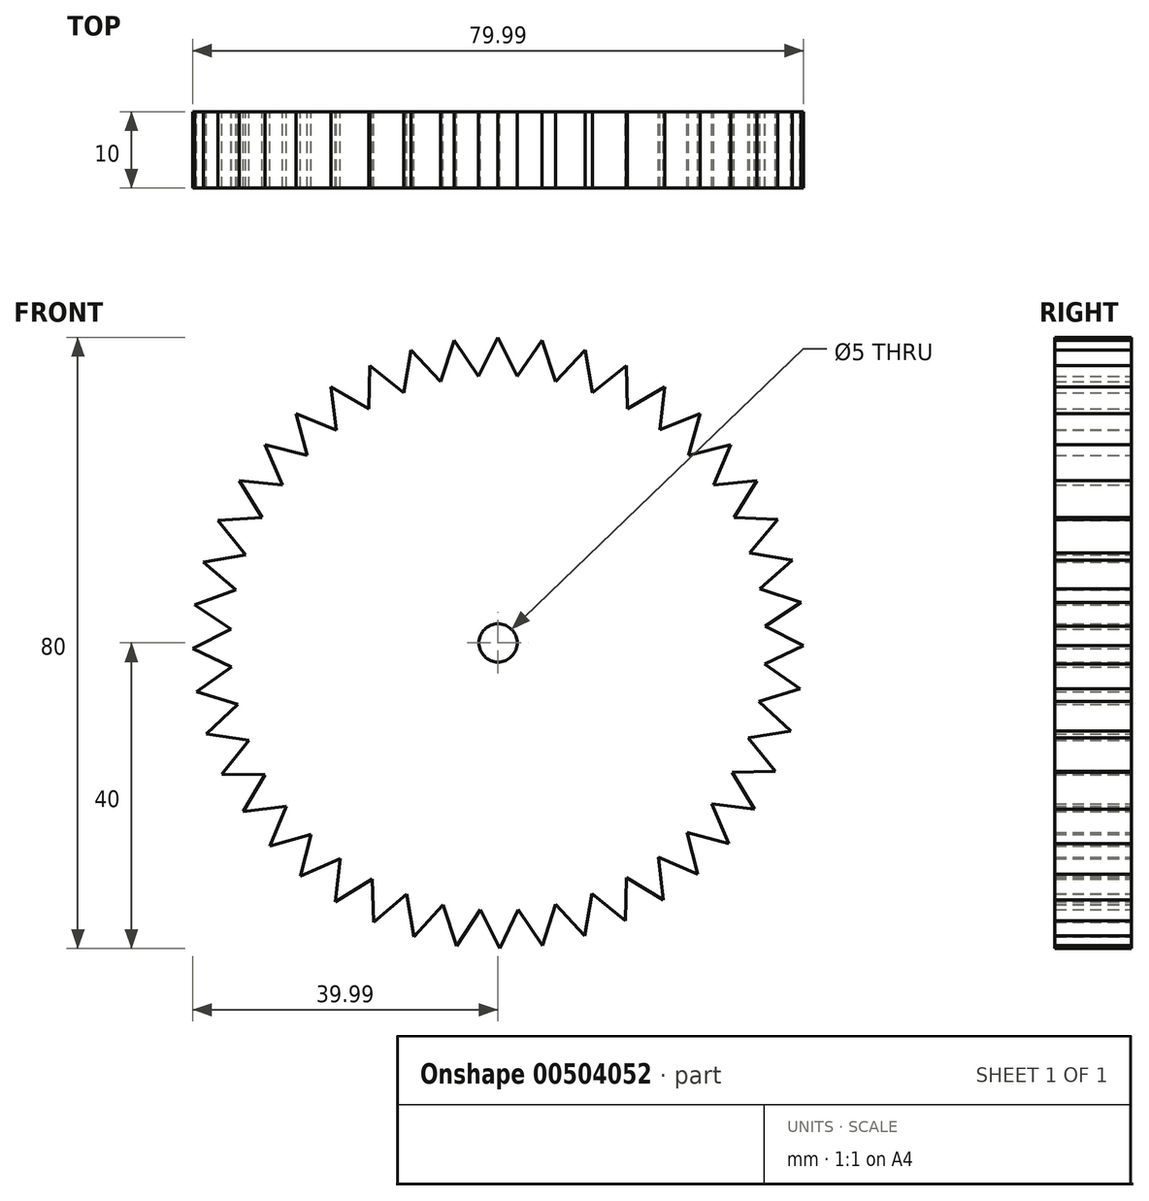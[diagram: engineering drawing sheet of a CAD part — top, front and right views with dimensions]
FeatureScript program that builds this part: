
annotation { "Feature Type Name" : "Feature", "Feature Type Description" : "" }
export const myFeature = defineFeature(function(context is Context, id is Id, definition is map)
    precondition{}
    {
        {
            var Q0;
            Q0=qCreatedBy(makeId("Front.planeOp"),FACE);
            var sketch = newSketch(context, id + "F0", { "sketchPlane" : qUnion([Q0])});
            skPoint(sketch, "E0.middle", {"position": v(0, 0) * mm});
            skCircle(sketch, "E1", {"center": v(0, 0) * mm, "radius": 40 * mm, "construction": true});
            skCircle(sketch, "E2", {"center": v(0, 0) * mm, "radius": 2.5 * mm});
            skLineSegment(sketch, "E3", {"start": v(0, 40) * mm, "end": v(2.52, 34.9) * mm});
            skLineSegment(sketch, "E4", {"start": v(2.52, 34.9) * mm, "end": v(5.75, 39.58) * mm});
            skLineSegment(sketch, "E5", {"start": v(5.75, 39.58) * mm, "end": v(7.52, 34.18) * mm});
            skLineSegment(sketch, "E6", {"start": v(7.52, 34.18) * mm, "end": v(11.39, 38.35) * mm});
            skLineSegment(sketch, "E7", {"start": v(11.39, 38.35) * mm, "end": v(12.36, 32.75) * mm});
            skLineSegment(sketch, "E8", {"start": v(12.36, 32.75) * mm, "end": v(16.78, 36.3) * mm});
            skLineSegment(sketch, "E9", {"start": v(16.78, 36.3) * mm, "end": v(16.94, 30.63) * mm});
            skLineSegment(sketch, "E10", {"start": v(16.94, 30.63) * mm, "end": v(21.83, 33.52) * mm});
            skLineSegment(sketch, "E11", {"start": v(21.83, 33.52) * mm, "end": v(21.17, 27.87) * mm});
            skLineSegment(sketch, "E12", {"start": v(21.17, 27.87) * mm, "end": v(26.42, 30.03) * mm});
            skLineSegment(sketch, "E13", {"start": v(26.42, 30.03) * mm, "end": v(24.95, 24.54) * mm});
            skCircle(sketch, "E14", {"center": v(0, 0) * mm, "radius": 35 * mm, "construction": true});
            skLineSegment(sketch, "E15", {"start": v(24.95, 24.54) * mm, "end": v(30.47, 25.92) * mm});
            skLineSegment(sketch, "E16", {"start": v(30.47, 25.92) * mm, "end": v(28.22, 20.7) * mm});
            skLineSegment(sketch, "E17", {"start": v(28.22, 20.7) * mm, "end": v(33.88, 21.27) * mm});
            skLineSegment(sketch, "E18", {"start": v(32.95, 11.8) * mm, "end": v(38.5, 10.85) * mm});
            skLineSegment(sketch, "E19", {"start": v(38.5, 10.85) * mm, "end": v(34.28, 7.09) * mm});
            skLineSegment(sketch, "E20", {"start": v(34.28, 7.09) * mm, "end": v(39.65, 5.3) * mm});
            skLineSegment(sketch, "E21", {"start": v(39.65, 5.3) * mm, "end": v(34.93, 2.18) * mm});
            skLineSegment(sketch, "E22", {"start": v(34.93, 2.18) * mm, "end": v(40, -0.34) * mm});
            skLineSegment(sketch, "E23", {"start": v(40, -0.34) * mm, "end": v(34.9, -2.77) * mm});
            skLineSegment(sketch, "E24", {"start": v(34.9, -2.77) * mm, "end": v(39.55, -5.98) * mm});
            skLineSegment(sketch, "E25", {"start": v(39.55, -5.98) * mm, "end": v(34.15, -7.67) * mm});
            skLineSegment(sketch, "E26", {"start": v(34.15, -7.67) * mm, "end": v(38.31, -11.5) * mm});
            skLineSegment(sketch, "E27", {"start": v(38.31, -11.5) * mm, "end": v(32.73, -12.4) * mm});
            skLineSegment(sketch, "E28", {"start": v(33.88, 21.27) * mm, "end": v(30.9, 16.42) * mm});
            skPoint(sketch, "E29.end.orphan", {"position": v(40, 0) * mm});
            skLineSegment(sketch, "E30", {"start": v(30.9, 16.42) * mm, "end": v(36.58, 16.17) * mm});
            skLineSegment(sketch, "E31", {"start": v(36.58, 16.17) * mm, "end": v(32.95, 11.8) * mm});
            skLineSegment(sketch, "E32", {"start": v(32.73, -12.4) * mm, "end": v(36.3, -16.79) * mm});
            skLineSegment(sketch, "E33", {"start": v(36.3, -16.79) * mm, "end": v(30.65, -16.9) * mm});
            skLineSegment(sketch, "E34", {"start": v(30.65, -16.9) * mm, "end": v(33.57, -21.74) * mm});
            skLineSegment(sketch, "E35", {"start": v(33.57, -21.74) * mm, "end": v(27.96, -21.06) * mm});
            skLineSegment(sketch, "E36", {"start": v(27.96, -21.06) * mm, "end": v(30.17, -26.26) * mm});
            skLineSegment(sketch, "E37", {"start": v(30.17, -26.26) * mm, "end": v(24.7, -24.8) * mm});
            skLineSegment(sketch, "E38", {"start": v(24.7, -24.8) * mm, "end": v(26.16, -30.26) * mm});
            skLineSegment(sketch, "E39", {"start": v(26.16, -30.26) * mm, "end": v(20.96, -28.03) * mm});
            skLineSegment(sketch, "E40", {"start": v(20.96, -28.03) * mm, "end": v(21.63, -33.65) * mm});
            skLineSegment(sketch, "E41", {"start": v(21.63, -33.65) * mm, "end": v(16.8, -30.7) * mm});
            skLineSegment(sketch, "E42", {"start": v(16.8, -30.7) * mm, "end": v(16.67, -36.36) * mm});
            skLineSegment(sketch, "E43", {"start": v(16.67, -36.36) * mm, "end": v(12.3, -32.77) * mm});
            skLineSegment(sketch, "E44", {"start": v(12.3, -32.77) * mm, "end": v(11.37, -38.35) * mm});
            skLineSegment(sketch, "E45", {"start": v(11.37, -38.35) * mm, "end": v(7.55, -34.18) * mm});
            skLineSegment(sketch, "E46", {"start": v(7.55, -34.18) * mm, "end": v(5.85, -39.57) * mm});
            skLineSegment(sketch, "E47", {"start": v(5.85, -39.57) * mm, "end": v(2.65, -34.9) * mm});
            skLineSegment(sketch, "E48", {"start": v(2.65, -34.9) * mm, "end": v(0.2, -40) * mm});
            skLineSegment(sketch, "E49", {"start": v(0.2, -40) * mm, "end": v(-2.3, -34.92) * mm});
            skLineSegment(sketch, "E50", {"start": v(-2.3, -34.92) * mm, "end": v(-5.44, -39.63) * mm});
            skLineSegment(sketch, "E51", {"start": v(-5.44, -39.63) * mm, "end": v(-7.2, -34.25) * mm});
            skLineSegment(sketch, "E52", {"start": v(-7.2, -34.25) * mm, "end": v(-10.98, -38.46) * mm});
            skLineSegment(sketch, "E53", {"start": v(-10.98, -38.46) * mm, "end": v(-11.96, -32.9) * mm});
            skLineSegment(sketch, "E54", {"start": v(-11.96, -32.9) * mm, "end": v(-16.3, -36.53) * mm});
            skLineSegment(sketch, "E55", {"start": v(-16.3, -36.53) * mm, "end": v(-16.48, -30.88) * mm});
            skLineSegment(sketch, "E56", {"start": v(-16.48, -30.88) * mm, "end": v(-21.29, -33.87) * mm});
            skLineSegment(sketch, "E57", {"start": v(-21.29, -33.87) * mm, "end": v(-20.67, -28.24) * mm});
            skLineSegment(sketch, "E58", {"start": v(-20.67, -28.24) * mm, "end": v(-25.85, -30.52) * mm});
            skLineSegment(sketch, "E59", {"start": v(-25.85, -30.52) * mm, "end": v(-24.45, -25.04) * mm});
            skLineSegment(sketch, "E60", {"start": v(-24.45, -25.04) * mm, "end": v(-29.9, -26.57) * mm});
            skLineSegment(sketch, "E61", {"start": v(-29.9, -26.57) * mm, "end": v(-27.74, -21.34) * mm});
            skLineSegment(sketch, "E62", {"start": v(-27.74, -21.34) * mm, "end": v(-33.35, -22.09) * mm});
            skLineSegment(sketch, "E63", {"start": v(-33.35, -22.09) * mm, "end": v(-30.47, -17.21) * mm});
            skLineSegment(sketch, "E64", {"start": v(-30.47, -17.21) * mm, "end": v(-36.13, -17.16) * mm});
            skLineSegment(sketch, "E65", {"start": v(-36.13, -17.16) * mm, "end": v(-32.6, -12.74) * mm});
            skLineSegment(sketch, "E66", {"start": v(-32.6, -12.74) * mm, "end": v(-38.2, -11.9) * mm});
            skLineSegment(sketch, "E67", {"start": v(-38.2, -11.9) * mm, "end": v(-34.07, -8.02) * mm});
            skLineSegment(sketch, "E68", {"start": v(-34.07, -8.02) * mm, "end": v(-39.49, -6.38) * mm});
            skLineSegment(sketch, "E69", {"start": v(-39.49, -6.38) * mm, "end": v(-34.86, -3.13) * mm});
            skLineSegment(sketch, "E70", {"start": v(-34.86, -3.13) * mm, "end": v(-40, -0.75) * mm});
            skLineSegment(sketch, "E71", {"start": v(-40, -0.75) * mm, "end": v(-34.95, 1.82) * mm});
            skLineSegment(sketch, "E72", {"start": v(-34.95, 1.82) * mm, "end": v(-39.68, 5.01) * mm});
            skLineSegment(sketch, "E73", {"start": v(-39.68, 5.01) * mm, "end": v(-34.3, 6.93) * mm});
            skLineSegment(sketch, "E74", {"start": v(-34.3, 6.93) * mm, "end": v(-38.58, 10.56) * mm});
            skLineSegment(sketch, "E75", {"start": v(-38.58, 10.56) * mm, "end": v(-33.05, 11.52) * mm});
            skLineSegment(sketch, "E76", {"start": v(-33.05, 11.52) * mm, "end": v(-36.66, 16) * mm});
            skLineSegment(sketch, "E77", {"start": v(-36.66, 16) * mm, "end": v(-30.91, 16.41) * mm});
            skLineSegment(sketch, "E78", {"start": v(-30.91, 16.41) * mm, "end": v(-33.89, 21.25) * mm});
            skLineSegment(sketch, "E79", {"start": v(-33.89, 21.25) * mm, "end": v(-28.23, 20.69) * mm});
            skLineSegment(sketch, "E80", {"start": v(-28.23, 20.69) * mm, "end": v(-30.48, 25.9) * mm});
            skLineSegment(sketch, "E81", {"start": v(-30.48, 25.9) * mm, "end": v(-24.96, 24.53) * mm});
            skLineSegment(sketch, "E82", {"start": v(-24.96, 24.53) * mm, "end": v(-26.43, 30.02) * mm});
            skLineSegment(sketch, "E83", {"start": v(-26.43, 30.02) * mm, "end": v(-21.18, 27.87) * mm});
            skLineSegment(sketch, "E84", {"start": v(-21.18, 27.87) * mm, "end": v(-21.84, 33.5) * mm});
            skLineSegment(sketch, "E85", {"start": v(-21.84, 33.5) * mm, "end": v(-16.95, 30.62) * mm});
            skLineSegment(sketch, "E86", {"start": v(-16.95, 30.62) * mm, "end": v(-16.8, 36.3) * mm});
            skLineSegment(sketch, "E87", {"start": v(-16.8, 36.3) * mm, "end": v(-12.37, 32.74) * mm});
            skLineSegment(sketch, "E88", {"start": v(-12.37, 32.74) * mm, "end": v(-11.4, 38.34) * mm});
            skLineSegment(sketch, "E89", {"start": v(-11.4, 38.34) * mm, "end": v(-7.53, 34.18) * mm});
            skLineSegment(sketch, "E90", {"start": v(-7.53, 34.18) * mm, "end": v(-5.77, 39.58) * mm});
            skLineSegment(sketch, "E91", {"start": v(-5.77, 39.58) * mm, "end": v(-2.54, 34.9) * mm});
            skLineSegment(sketch, "E92", {"start": v(-2.54, 34.9) * mm, "end": v(0, 40) * mm});
            skCircle(sketch, "E93", {"center": v(0, 0) * mm, "radius": 2 * mm});
            skSolve(sketch);
        }
        {
            var Q0;
            Q0=makeQuery(id+"F0.imprint","IMPRINT",FACE,{"disambiguationData":[TD([[makeQuery(id+"F0.imprint","IMPRINT",EDGE,{"derivedFrom":sQuery(id+"F0.wireOp",EDGE,"E2")}),-1.0]])]});
            extrude(context, id + "F1", {"entities" : qUnion([Q0]), "depth" : 10 * mm});
        }
    });
